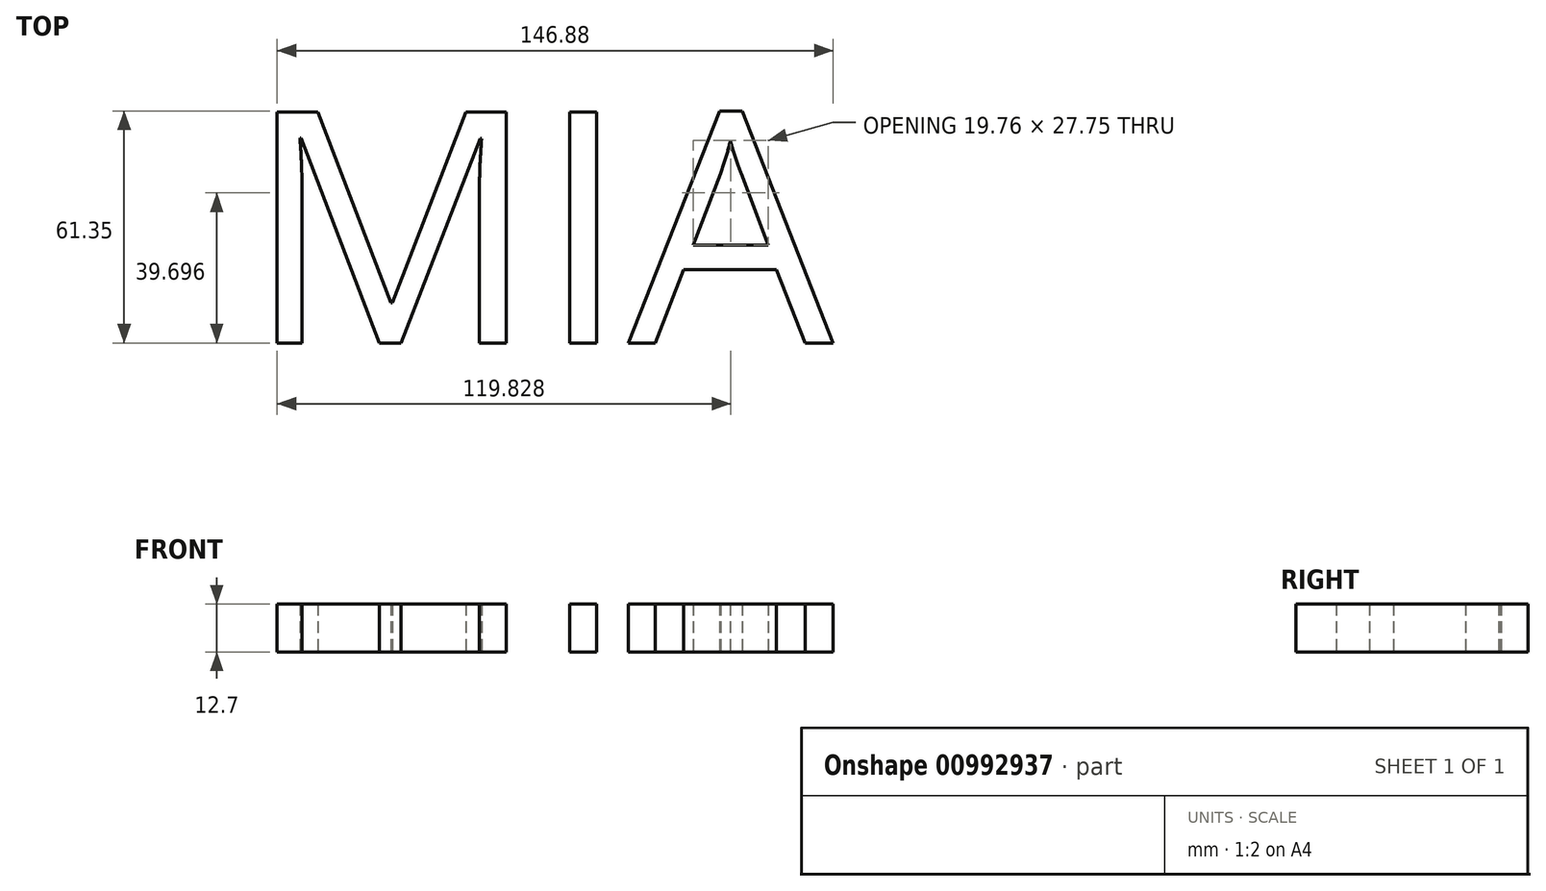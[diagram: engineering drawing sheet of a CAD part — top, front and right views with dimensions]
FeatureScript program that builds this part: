
annotation { "Feature Type Name" : "Feature", "Feature Type Description" : "" }
export const myFeature = defineFeature(function(context is Context, id is Id, definition is map)
    precondition{}
    {
        {
            var Q0;
            Q0=qCreatedBy(makeId("Top.planeOp"),FACE);
            var sketch = newSketch(context, id + "F0", { "sketchPlane" : qUnion([Q0])});
            skText(sketch, "E0", { "text": "MIA", "fontName": "OpenSans-Regular.ttf"});
            const initialGuessF0  = {"E0": [-0.0765, -0.02778, 1, 0, 0.06162]};
            skSetInitialGuess(sketch, initialGuessF0);
            skSolve(sketch);
        }
        {
            var Q0;
            Q0 = qSketchRegion(id + "F0", true);
            extrude(context, id + "F1", {"entities" : qUnion([Q0]), "depth" : 12.7 * mm, "offsetDistance" : 25.4 * mm});
        }
    });
